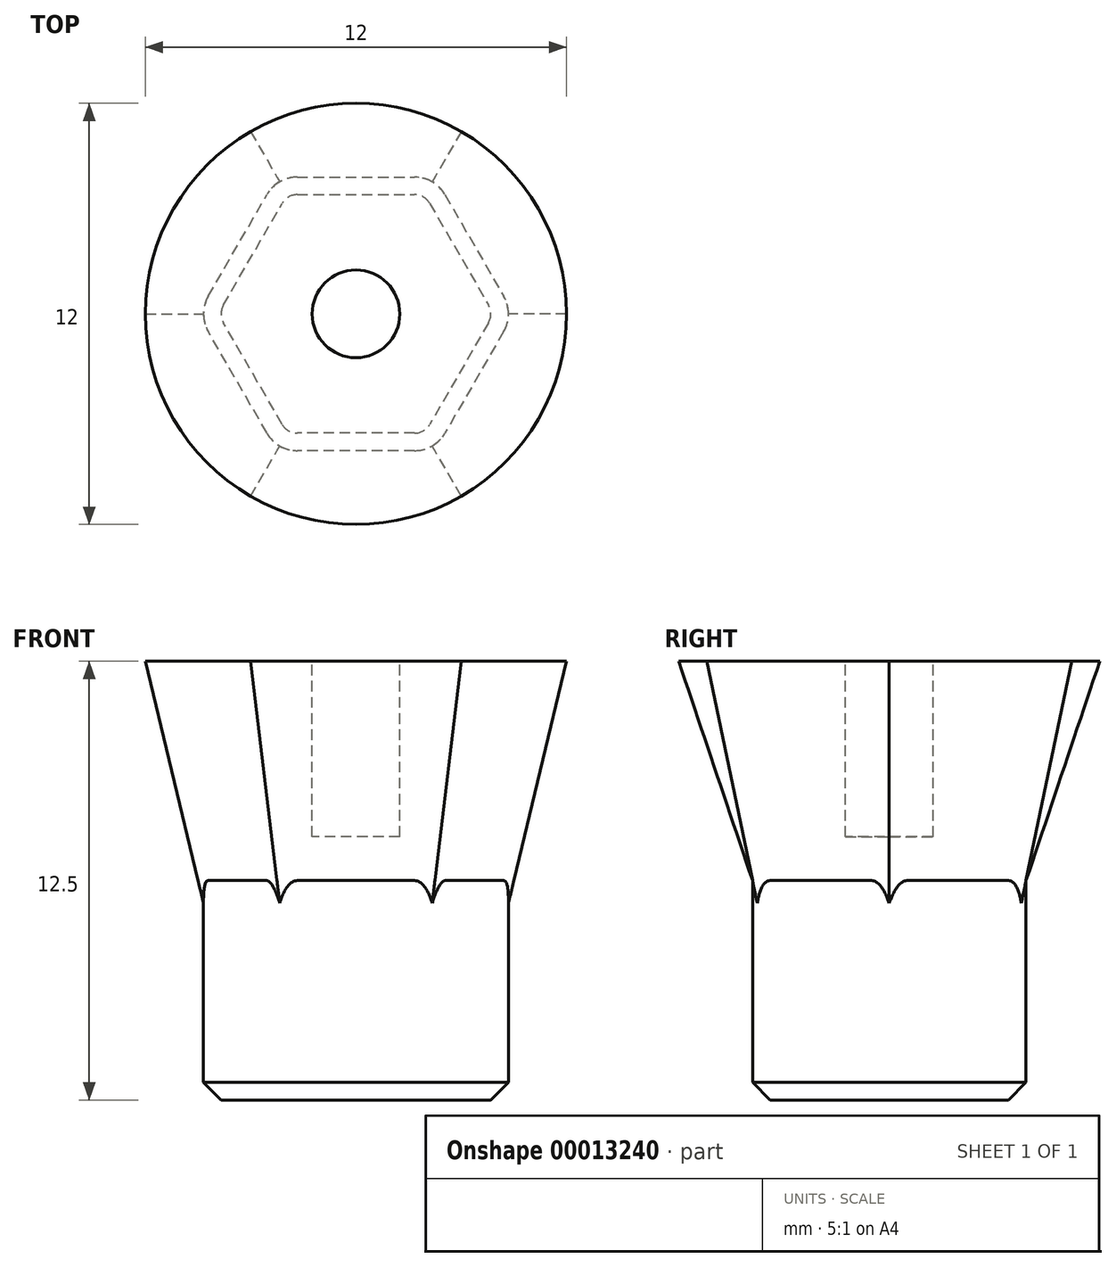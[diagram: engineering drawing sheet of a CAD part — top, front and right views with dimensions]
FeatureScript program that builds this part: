
annotation { "Feature Type Name" : "Feature", "Feature Type Description" : "" }
export const myFeature = defineFeature(function(context is Context, id is Id, definition is map)
    precondition{}
    {
        {
            var Q0;
            Q0=qCreatedBy(makeId("Top.planeOp"),FACE);
            var sketch = newSketch(context, id + "F0", { "sketchPlane" : qUnion([Q0])});
            skCircle(sketch, "E0.cCircle", {"center": v(0, 0) * mm, "radius": 3.9 * mm, "construction": true});
            skLineSegment(sketch, "E0.0", {"start": v(-2.25, 3.9) * mm, "end": v(2.25, 3.9) * mm});
            skLineSegment(sketch, "E0.1", {"start": v(2.25, 3.9) * mm, "end": v(4.5, 0) * mm});
            skLineSegment(sketch, "E0.2", {"start": v(4.5, 0) * mm, "end": v(2.25, -3.9) * mm});
            skLineSegment(sketch, "E0.3", {"start": v(2.25, -3.9) * mm, "end": v(-2.25, -3.9) * mm});
            skLineSegment(sketch, "E0.4", {"start": v(-2.25, -3.9) * mm, "end": v(-4.5, 0) * mm});
            skLineSegment(sketch, "E0.5", {"start": v(-4.5, 0) * mm, "end": v(-2.25, 3.9) * mm});
            skPoint(sketch, "E0.0.midPoint", {"position": v(0, 3.9) * mm});
            skSolve(sketch);
        }
        {
            var Q0;
            Q0=makeQuery(id+"F0.imprint","IMPRINT",FACE,{"disambiguationData":[TD([[makeQuery(id+"F0.imprint","IMPRINT",EDGE,{"derivedFrom":sQuery(id+"F0.wireOp",EDGE,"E0.0")}),-1.0]])]});
            cPlane(context, id + "F1", {"entities" : qUnion([Q0]), "cplaneType" : CPlaneType.OFFSET, "offset" : 6.25 * mm, "width" : 150 * mm, "height" : 150 * mm});
        }
        {
            var Q0;
            Q0=qCreatedBy(id+"F1.planeOp",FACE);
            var sketch = newSketch(context, id + "F2", { "sketchPlane" : qUnion([Q0])});
            skCircle(sketch, "E1", {"center": v(0, 0) * mm, "radius": 6 * mm});
            skSolve(sketch);
        }
        {
            var Q0;
            Q0 = qSketchRegion(id + "F2", true);
            var Q1;
            Q1 = qSketchRegion(id + "F0", true);
            loft(context, id + "F3", {"sheetProfilesArray" : [{ "sheetProfileEntities" : qUnion([Q0]) }, { "sheetProfileEntities" : qUnion([Q1]) }]});
        }
        {
            var Q0;
            Q0=makeQuery(id+"F3.opLoft","CAP_FACE",FACE,{"disambiguationData":[OSD([makeQuery(id+"F0.imprint","IMPRINT",FACE,{"disambiguationData":[TD([[makeQuery(id+"F0.imprint","IMPRINT",EDGE,{"derivedFrom":sQuery(id+"F0.wireOp",EDGE,"E0.0")}),-1.0]])]})])],"isStart":true});
            extrude(context, id + "F4", {"entities" : qUnion([Q0]), "operationType" : NewBodyOperationType.ADD, "depth" : 6.25 * mm});
        }
        {
            var Q0;
            Q0=makeQuery(id+"F3.opLoft","CAP_FACE",FACE,{"disambiguationData":[OSD([makeQuery(id+"F2.imprint","IMPRINT",FACE,{"disambiguationData":[TD([[makeQuery(id+"F2.imprint","IMPRINT",EDGE,{"derivedFrom":sQuery(id+"F2.wireOp",EDGE,"E1")}),1.0]])]})])],"isStart":true});
            var sketch = newSketch(context, id + "F5", { "sketchPlane" : qUnion([Q0])});
            skCircle(sketch, "E2", {"center": v(0, 0) * mm, "radius": 1.25 * mm});
            skSolve(sketch);
        }
        {
            var Q0;
            Q0 = qSketchRegion(id + "F5", true);
            extrude(context, id + "F6", {"entities" : qUnion([Q0]), "operationType" : NewBodyOperationType.REMOVE, "oppositeDirection" : true, "depth" : 5 * mm});
        }
        {
            var Q0;
            Q0=makeQuery(id+"F4.opExtrude","SWEPT_EDGE",EDGE,{"disambiguationData":[OSD([sQuery(id+"F0.wireOp",EDGE,"E0.1"),sQuery(id+"F0.wireOp",EDGE,"E0.2")])]});
            var Q1;
            Q1=makeQuery(id+"F4.opExtrude","SWEPT_EDGE",EDGE,{"disambiguationData":[OSD([sQuery(id+"F0.wireOp",EDGE,"E0.2"),sQuery(id+"F0.wireOp",EDGE,"E0.3")])]});
            var Q2;
            Q2=makeQuery(id+"F4.opExtrude","SWEPT_EDGE",EDGE,{"disambiguationData":[OSD([sQuery(id+"F0.wireOp",EDGE,"E0.3"),sQuery(id+"F0.wireOp",EDGE,"E0.4")])]});
            var Q3;
            Q3=makeQuery(id+"F4.opExtrude","SWEPT_EDGE",EDGE,{"disambiguationData":[OSD([sQuery(id+"F0.wireOp",EDGE,"E0.4"),sQuery(id+"F0.wireOp",EDGE,"E0.5")])]});
            var Q4;
            Q4=makeQuery(id+"F4.opExtrude","SWEPT_EDGE",EDGE,{"disambiguationData":[OSD([sQuery(id+"F0.wireOp",EDGE,"E0.0"),sQuery(id+"F0.wireOp",EDGE,"E0.5")])]});
            var Q5;
            Q5=makeQuery(id+"F4.opExtrude","SWEPT_EDGE",EDGE,{"disambiguationData":[OSD([sQuery(id+"F0.wireOp",EDGE,"E0.0"),sQuery(id+"F0.wireOp",EDGE,"E0.1")])]});
            fillet(context, id + "F7", {"entities" : qUnion([Q0, Q1, Q2, Q3, Q4, Q5]), "radius" : 1 * mm, "tangentPropagation" : true, "allowEdgeOverflow" : false});
        }
        {
            var Q0;
            Q0=makeQuery(id+"F4.opExtrude","CAP_EDGE",EDGE,{"disambiguationData":[OSD([sQuery(id+"F0.wireOp",EDGE,"E0.0"),sQuery(id+"F0.wireOp",EDGE,"E0.4"),sQuery(id+"F0.wireOp",EDGE,"E0.5")])],"isStart":false});
            chamfer(context, id + "F8", {"entities" : qUnion([Q0]), "width" : .5 * mm, "tangentPropagation" : true});
        }
    });
